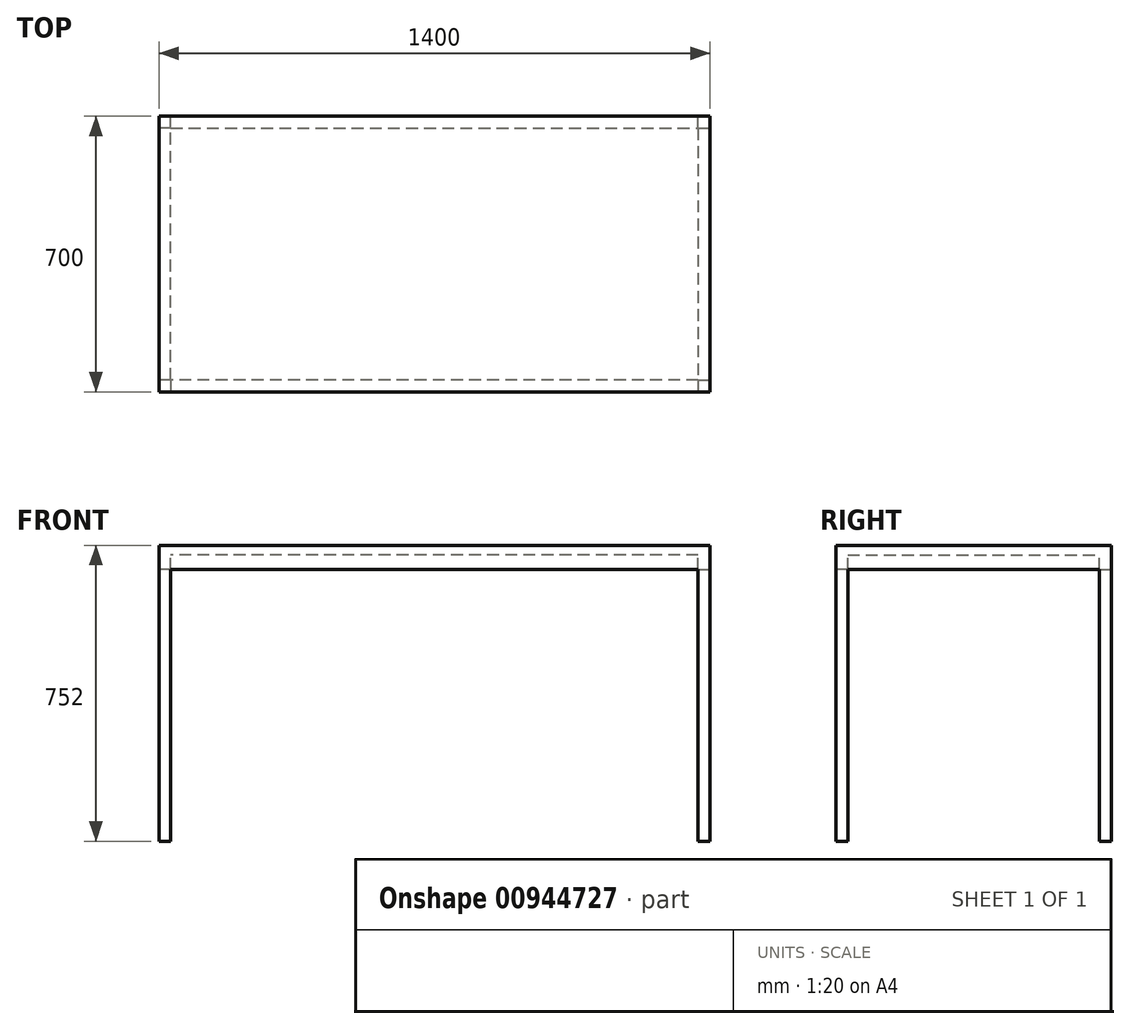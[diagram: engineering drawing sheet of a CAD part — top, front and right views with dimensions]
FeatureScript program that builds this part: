
annotation { "Feature Type Name" : "Feature", "Feature Type Description" : "" }
export const myFeature = defineFeature(function(context is Context, id is Id, definition is map)
    precondition{}
    {
        {
            var Q0;
            Q0=qCreatedBy(makeId("Top.planeOp"),FACE);
            var sketch = newSketch(context, id + "F0", { "sketchPlane" : qUnion([Q0])});
            skLineSegment(sketch, "E0.bottom", {"start": v(0, 0) * mm, "end": v(1400, 0) * mm});
            skLineSegment(sketch, "E0.top", {"start": v(0, -700) * mm, "end": v(1400, -700) * mm});
            skLineSegment(sketch, "E0.left", {"start": v(0, 0) * mm, "end": v(0, -700) * mm});
            skLineSegment(sketch, "E0.right", {"start": v(1400, 0) * mm, "end": v(1400, -700) * mm});
            skSolve(sketch);
        }
        {
            var Q0;
            Q0 = qSketchRegion(id + "F0", true);
            extrude(context, id + "F1", {"entities" : qUnion([Q0]), "oppositeDirection" : true, "depth" : 25 * mm, "offsetDistance" : 25 * mm});
        }
        {
            var Q0;
            Q0=makeQuery(id+"F1.opExtrude","CAP_FACE",FACE,{"disambiguationData":[OSD([sQuery(id+"F0.wireOp",EDGE,"E0.bottom"),sQuery(id+"F0.wireOp",EDGE,"E0.top"),sQuery(id+"F0.wireOp",EDGE,"E0.left"),sQuery(id+"F0.wireOp",EDGE,"E0.right")])],"isStart":false});
            var sketch = newSketch(context, id + "F2", { "sketchPlane" : qUnion([Q0])});
            skLineSegment(sketch, "E1.bottom", {"start": v(0, 0) * mm, "end": v(1400, 0) * mm});
            skLineSegment(sketch, "E1.top", {"start": v(0, 700) * mm, "end": v(1400, 700) * mm});
            skLineSegment(sketch, "E1.left", {"start": v(0, 0) * mm, "end": v(0, 700) * mm});
            skLineSegment(sketch, "E1.right", {"start": v(1400, 0) * mm, "end": v(1400, 700) * mm});
            skLineSegment(sketch, "E2.0", {"start": v(30, 670) * mm, "end": v(30, 30) * mm});
            skLineSegment(sketch, "E2.1", {"start": v(1370, 670) * mm, "end": v(30, 670) * mm});
            skLineSegment(sketch, "E2.2", {"start": v(1370, 30) * mm, "end": v(1370, 670) * mm});
            skLineSegment(sketch, "E2.3", {"start": v(30, 30) * mm, "end": v(1370, 30) * mm});
            skSolve(sketch);
        }
        {
            var Q0;
            Q0 = qSketchRegion(id + "F2", true);
            extrude(context, id + "F3", {"entities" : qUnion([Q0]), "operationType" : NewBodyOperationType.ADD, "depth" : 37 * mm, "offsetDistance" : 25 * mm});
        }
        {
            var Q0;
            Q0=makeQuery(id+"F3.opExtrude","CAP_FACE",FACE,{"disambiguationData":[OSD([sQuery(id+"F2.wireOp",EDGE,"E1.bottom"),sQuery(id+"F2.wireOp",EDGE,"E1.top"),sQuery(id+"F2.wireOp",EDGE,"E1.left"),sQuery(id+"F2.wireOp",EDGE,"E1.right"),sQuery(id+"F2.wireOp",EDGE,"E2.0"),sQuery(id+"F2.wireOp",EDGE,"E2.1"),sQuery(id+"F2.wireOp",EDGE,"E2.2"),sQuery(id+"F2.wireOp",EDGE,"E2.3")])],"isStart":false});
            var sketch = newSketch(context, id + "F4", { "sketchPlane" : qUnion([Q0])});
            skLineSegment(sketch, "E3.bottom", {"start": v(30, 670) * mm, "end": v(0, 670) * mm});
            skLineSegment(sketch, "E3.top", {"start": v(30, 700) * mm, "end": v(0, 700) * mm});
            skLineSegment(sketch, "E3.left", {"start": v(30, 670) * mm, "end": v(30, 700) * mm});
            skLineSegment(sketch, "E3.right", {"start": v(0, 670) * mm, "end": v(0, 700) * mm});
            skLineSegment(sketch, "E4.bottom", {"start": v(30, 30) * mm, "end": v(0, 30) * mm});
            skLineSegment(sketch, "E4.top", {"start": v(30, 0) * mm, "end": v(0, 0) * mm});
            skLineSegment(sketch, "E4.left", {"start": v(30, 30) * mm, "end": v(30, 0) * mm});
            skLineSegment(sketch, "E4.right", {"start": v(0, 30) * mm, "end": v(0, 0) * mm});
            skLineSegment(sketch, "E5.bottom", {"start": v(1370, 670) * mm, "end": v(1400, 670) * mm});
            skLineSegment(sketch, "E5.top", {"start": v(1370, 700) * mm, "end": v(1400, 700) * mm});
            skLineSegment(sketch, "E5.left", {"start": v(1370, 670) * mm, "end": v(1370, 700) * mm});
            skLineSegment(sketch, "E5.right", {"start": v(1400, 670) * mm, "end": v(1400, 700) * mm});
            skLineSegment(sketch, "E6.bottom", {"start": v(1370, 30) * mm, "end": v(1400, 30) * mm});
            skLineSegment(sketch, "E6.top", {"start": v(1370, 0) * mm, "end": v(1400, 0) * mm});
            skLineSegment(sketch, "E6.left", {"start": v(1370, 30) * mm, "end": v(1370, 0) * mm});
            skLineSegment(sketch, "E6.right", {"start": v(1400, 30) * mm, "end": v(1400, 0) * mm});
            skSolve(sketch);
        }
        {
            var Q0;
            Q0 = qSketchRegion(id + "F4", true);
            extrude(context, id + "F5", {"entities" : qUnion([Q0]), "operationType" : NewBodyOperationType.ADD, "depth" : 690 * mm, "offsetDistance" : 25 * mm});
        }
    });
